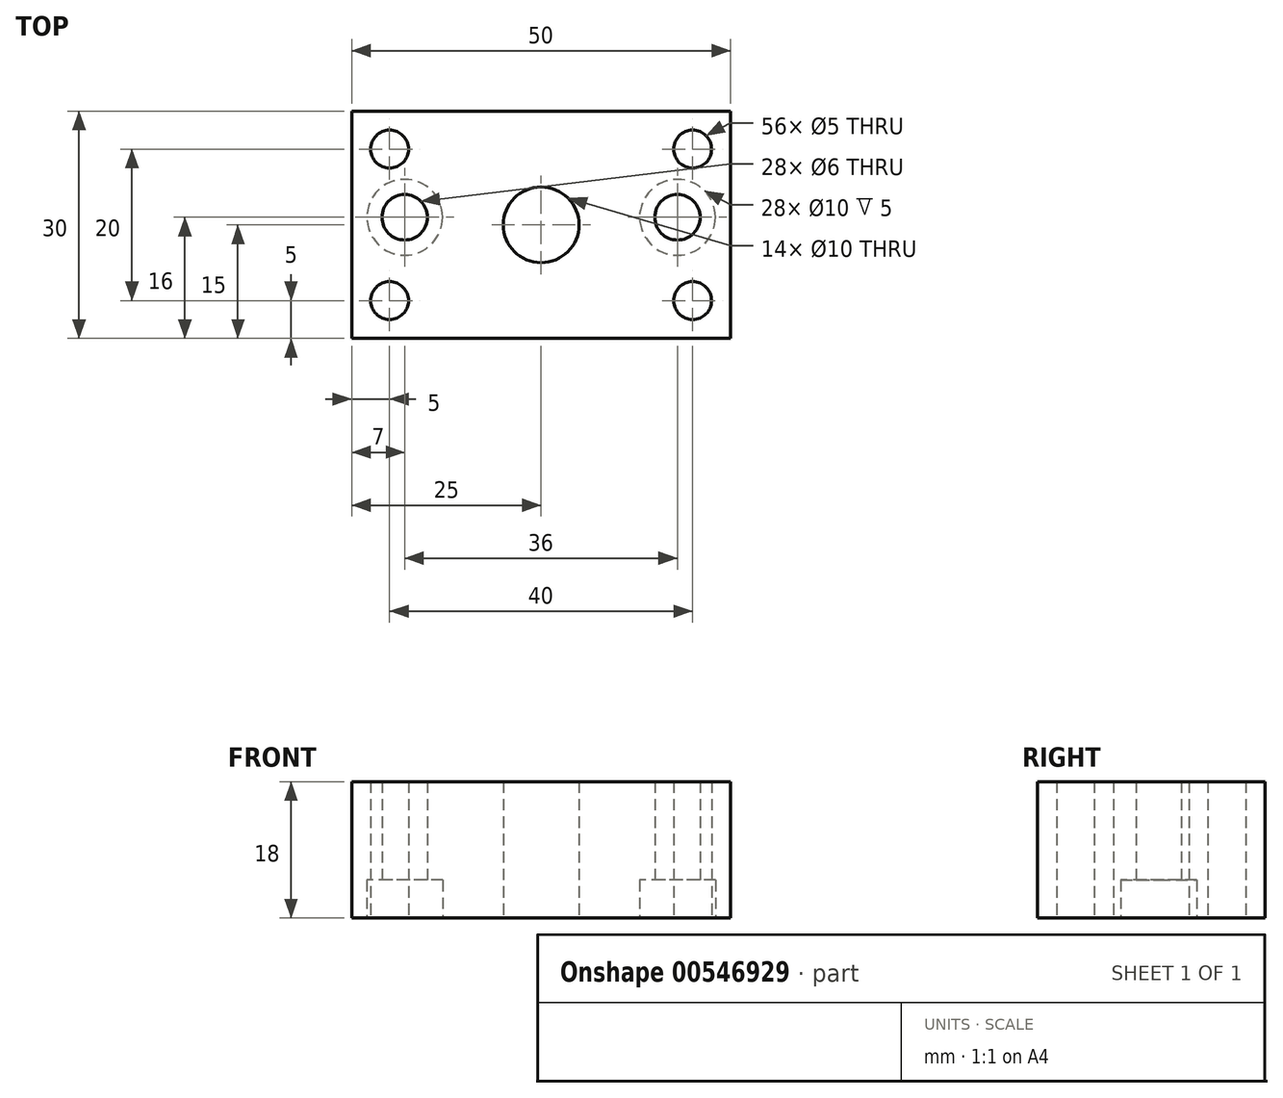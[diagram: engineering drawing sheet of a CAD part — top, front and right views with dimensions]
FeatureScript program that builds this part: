
annotation { "Feature Type Name" : "Feature", "Feature Type Description" : "" }
export const myFeature = defineFeature(function(context is Context, id is Id, definition is map)
    precondition{}
    {
        {
            var Q0;
            Q0=qCreatedBy(makeId("Top.planeOp"),FACE);
            var sketch = newSketch(context, id + "F0", { "sketchPlane" : qUnion([Q0])});
            skLineSegment(sketch, "E0.bottom", {"start": v(0, 0) * mm, "end": v(50, 0) * mm});
            skLineSegment(sketch, "E0.top", {"start": v(0, -30) * mm, "end": v(50, -30) * mm});
            skLineSegment(sketch, "E0.left", {"start": v(0, 0) * mm, "end": v(0, -30) * mm});
            skLineSegment(sketch, "E0.right", {"start": v(50, 0) * mm, "end": v(50, -30) * mm});
            skLineSegment(sketch, "E1", {"start": v(0, 0) * mm, "end": v(0, -15) * mm, "construction": true});
            skLineSegment(sketch, "E2", {"start": v(0, -15) * mm, "end": v(50, -15) * mm, "construction": true});
            skLineSegment(sketch, "E3", {"start": v(50, -15) * mm, "end": v(25, -15) * mm, "construction": true});
            skLineSegment(sketch, "E4", {"start": v(25, -15) * mm, "end": v(25, -29) * mm, "construction": true});
            skLineSegment(sketch, "E5.0", {"start": v(7, -14) * mm, "end": v(7, -28) * mm, "construction": true});
            skLineSegment(sketch, "E6.0", {"start": v(43, -14) * mm, "end": v(43, -28) * mm, "construction": true});
            skCircle(sketch, "E7", {"center": v(25, -15) * mm, "radius": 5 * mm});
            skCircle(sketch, "E8", {"center": v(7, -14) * mm, "radius": 3 * mm});
            skCircle(sketch, "E9", {"center": v(43, -14) * mm, "radius": 3 * mm});
            skCircle(sketch, "E10", {"center": v(7, -14) * mm, "radius": 5 * mm});
            skCircle(sketch, "E11", {"center": v(43, -14) * mm, "radius": 5 * mm});
            skLineSegment(sketch, "E12.0", {"start": v(5, -5) * mm, "end": v(45, -5) * mm, "construction": true});
            skLineSegment(sketch, "E13.0", {"start": v(5, -25) * mm, "end": v(45, -25) * mm, "construction": true});
            skLineSegment(sketch, "E14.0", {"start": v(5, -5) * mm, "end": v(5, -25) * mm, "construction": true});
            skLineSegment(sketch, "E15.0", {"start": v(45, -5) * mm, "end": v(45, -25) * mm, "construction": true});
            skCircle(sketch, "E16", {"center": v(5, -5) * mm, "radius": 2.5 * mm});
            skCircle(sketch, "E17", {"center": v(45, -5) * mm, "radius": 2.5 * mm});
            skCircle(sketch, "E18", {"center": v(45, -25) * mm, "radius": 2.5 * mm});
            skCircle(sketch, "E19", {"center": v(5, -25) * mm, "radius": 2.5 * mm});
            skSolve(sketch);
        }
        {
            var Q0;
            Q0=makeQuery(id+"F0.imprint","IMPRINT",FACE,{"disambiguationData":[TD([[makeQuery(id+"F0.imprint","IMPRINT",EDGE,{"derivedFrom":sQuery(id+"F0.wireOp",EDGE,"E8")}),-1.0]])]});
            var Q1;
            Q1=makeQuery(id+"F0.imprint","IMPRINT",FACE,{"disambiguationData":[TD([[makeQuery(id+"F0.imprint","IMPRINT",EDGE,{"derivedFrom":sQuery(id+"F0.wireOp",EDGE,"E9")}),-1.0]])]});
            var Q2;
            Q2=makeQuery(id+"F0.imprint","IMPRINT",FACE,{"disambiguationData":[TD([[makeQuery(id+"F0.imprint","IMPRINT",EDGE,{"derivedFrom":sQuery(id+"F0.wireOp",EDGE,"E0.bottom")}),-1.0]])]});
            extrude(context, id + "F1", {"entities" : qUnion([Q0, Q1, Q2]), "depth" : 18 * mm, "offsetDistance" : 25 * mm});
        }
        {
            var Q0;
            Q0=makeQuery(id+"F0.imprint","IMPRINT",FACE,{"disambiguationData":[TD([[makeQuery(id+"F0.imprint","IMPRINT",EDGE,{"derivedFrom":sQuery(id+"F0.wireOp",EDGE,"E8")}),-1.0]])]});
            var Q1;
            Q1=makeQuery(id+"F0.imprint","IMPRINT",FACE,{"disambiguationData":[TD([[makeQuery(id+"F0.imprint","IMPRINT",EDGE,{"derivedFrom":sQuery(id+"F0.wireOp",EDGE,"E9")}),-1.0]])]});
            extrude(context, id + "F2", {"entities" : qUnion([Q0, Q1]), "operationType" : NewBodyOperationType.REMOVE, "depth" : 5 * mm, "offsetDistance" : 25 * mm});
        }
    });
